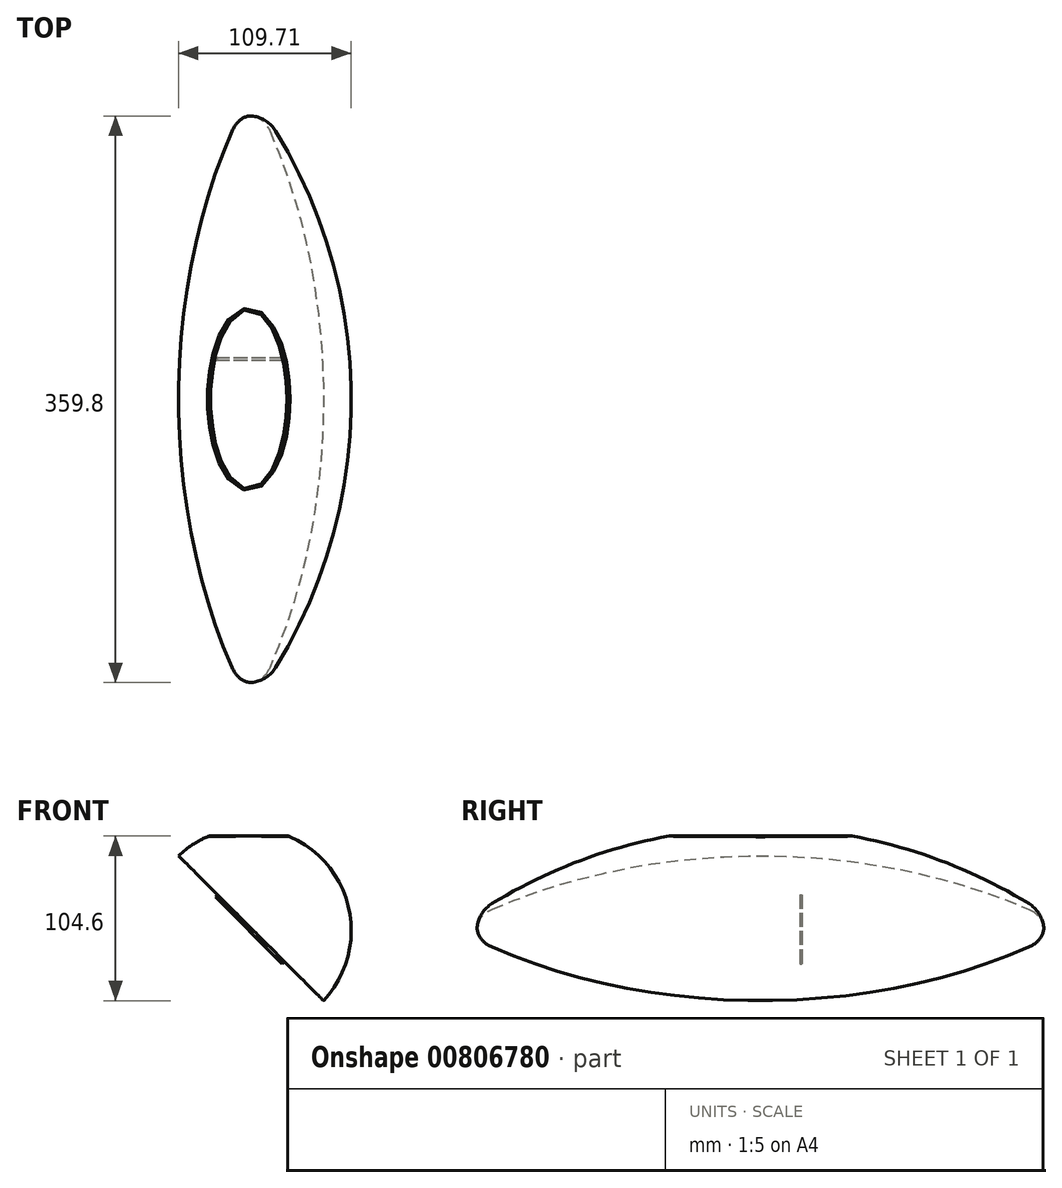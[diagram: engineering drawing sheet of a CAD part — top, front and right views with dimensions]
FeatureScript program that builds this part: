
annotation { "Feature Type Name" : "Feature", "Feature Type Description" : "" }
export const myFeature = defineFeature(function(context is Context, id is Id, definition is map)
    precondition{}
    {
        {
            var Q0;
            Q0=qCreatedBy(makeId("Right.planeOp"),FACE);
            var sketch = newSketch(context, id + "F0", { "sketchPlane" : qUnion([Q0])});
            skLineSegment(sketch, "E0", {"start": v(-180, 0) * mm, "end": v(180, 0) * mm});
            skArc(sketch, "E1", {"start": v(-170.45, 17.06) * mm, "mid": v(-177.45, 9.77) * mm, "end": v(-180, 0) * mm});
            skArc(sketch, "E2", {"start": v(180, 0) * mm, "mid": v(177.45, 9.77) * mm, "end": v(170.45, 17.06) * mm});
            skLineSegment(sketch, "E3", {"start": v(-180, 0) * mm, "end": v(-180, -15) * mm, "construction": true});
            skLineSegment(sketch, "E4", {"start": v(180, 0) * mm, "end": v(180, -15) * mm, "construction": true});
            skLineSegment(sketch, "E5", {"start": v(-57.5, 60) * mm, "end": v(57.5, 60) * mm, "construction": true});
            skLineSegment(sketch, "E6", {"start": v(0, 60) * mm, "end": v(0, 0) * mm, "construction": true});
            skArc(sketch, "E7", {"start": v(170.45, 17.06) * mm, "mid": v(0, 65.1) * mm, "end": v(-170.45, 17.06) * mm});
            skSolve(sketch);
        }
        {
            var Q0;
            Q0=qSketchRegion(id+"F0",true);
            var Q1;
            Q1=sQuery(id+"F0.wireOp",EDGE,"E0");
            revolve(context, id + "F1", {"surfaceOperationType" : NewSurfaceOperationType.NEW, "entities" : qUnion([Q0]), "axis" : qUnion([Q1]), "revolveType" : RevolveType.FULL});
        }
        {
            var Q0;
            Q0=qCreatedBy(makeId("Right.planeOp"),FACE);
            var sketch = newSketch(context, id + "F2", { "sketchPlane" : qUnion([Q0])});
            skLineSegment(sketch, "E8.bottom", {"start": v(-75, -70) * mm, "end": v(75, -70) * mm});
            skLineSegment(sketch, "E8.top", {"start": v(-75, -60) * mm, "end": v(75, -60) * mm});
            skLineSegment(sketch, "E8.left", {"start": v(-75, -70) * mm, "end": v(-75, -60) * mm});
            skLineSegment(sketch, "E8.right", {"start": v(75, -70) * mm, "end": v(75, -60) * mm});
            skLineSegment(sketch, "E9.bottom", {"start": v(-75, 70) * mm, "end": v(75, 70) * mm});
            skLineSegment(sketch, "E9.top", {"start": v(-75, 60) * mm, "end": v(75, 60) * mm});
            skLineSegment(sketch, "E9.left", {"start": v(-75, 70) * mm, "end": v(-75, 60) * mm});
            skLineSegment(sketch, "E9.right", {"start": v(75, 70) * mm, "end": v(75, 60) * mm});
            skLineSegment(sketch, "E10", {"start": v(-170.45, 0) * mm, "end": v(170.45, 0) * mm});
            skLineSegment(sketch, "E11", {"start": v(0, 60) * mm, "end": v(0, 0) * mm});
            skSolve(sketch);
        }
        {
            var Q0;
            Q0=qSketchRegion(id+"F2",true);
            extrude(context, id + "F3", {"entities" : qUnion([Q0]), "operationType" : NewBodyOperationType.REMOVE, "endBound" : BoundingType.SYMMETRIC, "depth" : 100 * mm, "offsetDistance" : 25 * mm});
        }
        {
            var Q0;
            Q0=qCreatedBy(makeId("Front.planeOp"),FACE);
            var sketch = newSketch(context, id + "F4", { "sketchPlane" : qUnion([Q0])});
            skLineSegment(sketch, "E12", {"start": v(-68.94, 68.94) * mm, "end": v(68.94, -68.94) * mm});
            skLineSegment(sketch, "E13", {"start": v(-68.94, 68.94) * mm, "end": v(-68.94, -68.94) * mm});
            skLineSegment(sketch, "E14", {"start": v(-68.94, -68.94) * mm, "end": v(68.94, -68.94) * mm});
            skSolve(sketch);
        }
        {
            var Q0;
            Q0=qSketchRegion(id+"F4",true);
            extrude(context, id + "F5", {"entities" : qUnion([Q0]), "operationType" : NewBodyOperationType.REMOVE, "endBound" : BoundingType.SYMMETRIC, "oppositeDirection" : true, "depth" : 406 * mm, "offsetDistance" : 25 * mm});
        }
        {
            var Q0;
            Q0=makeQuery(id+"F5.boolean.opBoolean","COPY",FACE,{"derivedFrom":makeQuery(id+"F5.opExtrude","SWEPT_FACE",FACE,{"disambiguationData":[OSD([sQuery(id+"F4.wireOp",EDGE,"E12")])]})});
            var sketch = newSketch(context, id + "F6", { "sketchPlane" : qUnion([Q0])});
            skLineSegment(sketch, "E15.bottom", {"start": v(-25, 30) * mm, "end": v(-26.5, 30) * mm});
            skLineSegment(sketch, "E15.top", {"start": v(-25, -30) * mm, "end": v(-26.5, -30) * mm});
            skLineSegment(sketch, "E15.left", {"start": v(-25, 30) * mm, "end": v(-25, -30) * mm});
            skLineSegment(sketch, "E15.right", {"start": v(-26.5, 30) * mm, "end": v(-26.5, -30) * mm});
            skLineSegment(sketch, "E16", {"start": v(0, 0) * mm, "end": v(-25, 0) * mm, "construction": true});
            skSolve(sketch);
        }
        {
            var Q0;
            Q0=makeQuery(id+"F6.imprint","IMPRINT",FACE,{"disambiguationData":[TD([[makeQuery(id+"F6.imprint","IMPRINT",EDGE,{"derivedFrom":sQuery(id+"F6.wireOp",EDGE,"E15.bottom")}),-1.0]])]});
            extrude(context, id + "F7", {"entities" : qUnion([Q0]), "operationType" : NewBodyOperationType.REMOVE, "oppositeDirection" : true, "depth" : 2 * mm, "offsetDistance" : 25 * mm});
        }
        {
            var Q0;
            Q0=makeQuery(id+"F3.boolean.opBoolean","INTERSECT",EDGE,{"derivedFrom":[makeQuery(id+"F1.opRevolve","SWEPT_FACE",FACE,{"disambiguationData":[OSD([sQuery(id+"F0.wireOp",EDGE,"E7")])]}),makeQuery(id+"F3.opExtrude","SWEPT_FACE",FACE,{"disambiguationData":[OSD([sQuery(id+"F2.wireOp",EDGE,"E9.top")])]})]});
            fillet(context, id + "F8", {"entities" : qUnion([Q0]), "radius" : 5 * mm, "tangentPropagation" : true, "allowEdgeOverflow" : false});
        }
    });
